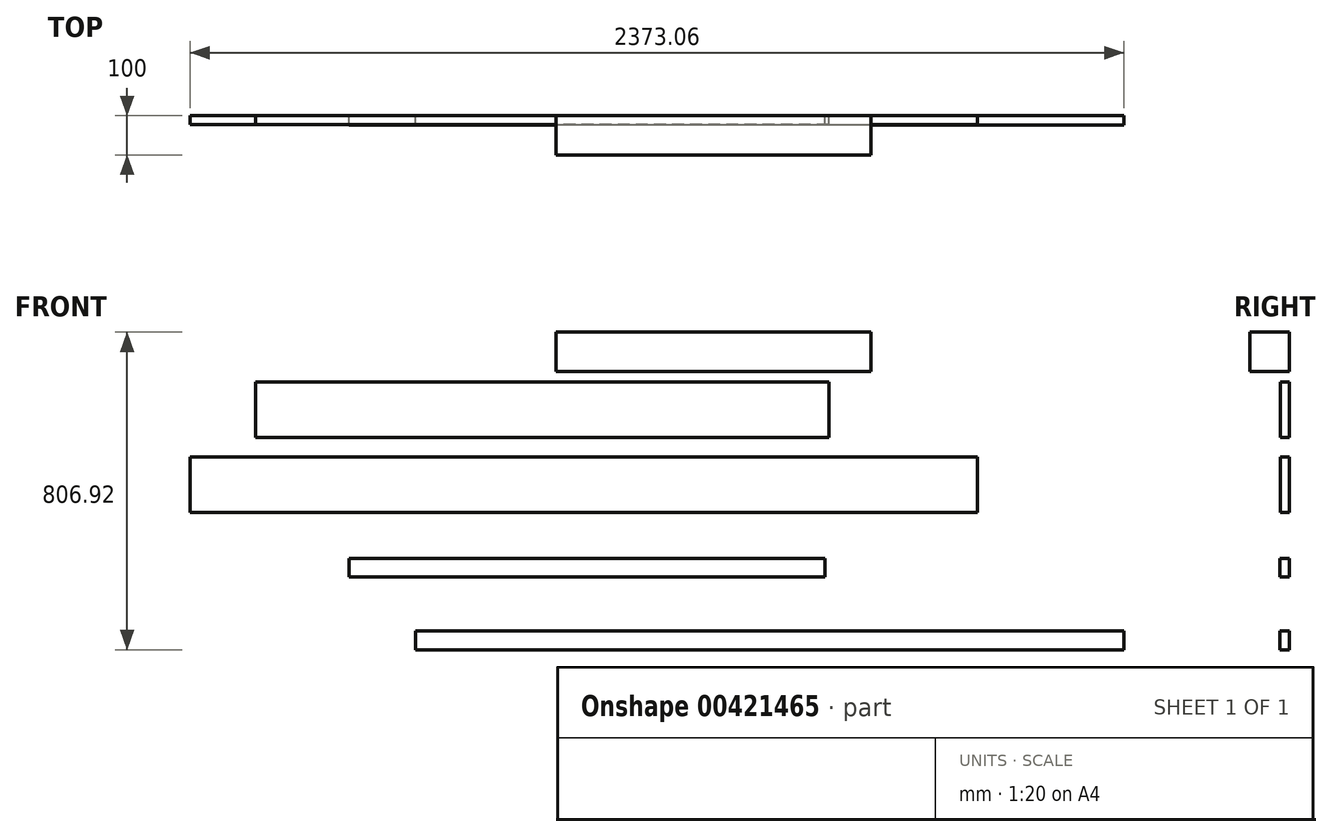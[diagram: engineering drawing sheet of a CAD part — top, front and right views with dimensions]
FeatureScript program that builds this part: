
annotation { "Feature Type Name" : "Feature", "Feature Type Description" : "" }
export const myFeature = defineFeature(function(context is Context, id is Id, definition is map)
    precondition{}
    {
        {
            var Q0;
            Q0=qCreatedBy(makeId("Front.planeOp"),FACE);
            var sketch = newSketch(context, id + "F0", { "sketchPlane" : qUnion([Q0])});
            skLineSegment(sketch, "E0.bottom", {"start": v(-999.75, 98.52) * mm, "end": v(1000.25, 98.52) * mm});
            skLineSegment(sketch, "E0.top", {"start": v(-999.75, -41.48) * mm, "end": v(1000.25, -41.48) * mm});
            skLineSegment(sketch, "E0.left", {"start": v(-999.75, 98.52) * mm, "end": v(-999.75, -41.48) * mm});
            skLineSegment(sketch, "E0.right", {"start": v(1000.25, 98.52) * mm, "end": v(1000.25, -41.48) * mm});
            skSolve(sketch);
        }
        {
            var Q0;
            Q0=makeQuery(id+"F0.imprint","IMPRINT",FACE,{"disambiguationData":[TD([[makeQuery(id+"F0.imprint","IMPRINT",EDGE,{"derivedFrom":sQuery(id+"F0.wireOp",EDGE,"E0.bottom")}),-1.0]])]});
            extrude(context, id + "F1", {"entities" : qUnion([Q0]), "depth" : 23 * mm});
        }
        {
            var Q0;
            Q0=qCreatedBy(makeId("Front.planeOp"),FACE);
            var sketch = newSketch(context, id + "F2", { "sketchPlane" : qUnion([Q0])});
            skLineSegment(sketch, "E1.bottom", {"start": v(623.06, 288.83) * mm, "end": v(-832.94, 288.83) * mm});
            skLineSegment(sketch, "E1.top", {"start": v(623.06, 148.83) * mm, "end": v(-832.94, 148.83) * mm});
            skLineSegment(sketch, "E1.left", {"start": v(623.06, 288.83) * mm, "end": v(623.06, 148.83) * mm});
            skLineSegment(sketch, "E1.right", {"start": v(-832.94, 288.83) * mm, "end": v(-832.94, 148.83) * mm});
            skSolve(sketch);
        }
        {
            var Q0;
            Q0 = qSketchRegion(id + "F2", true);
            extrude(context, id + "F3", {"entities" : qUnion([Q0]), "depth" : 23 * mm});
        }
        {
            var Q0;
            Q0=qCreatedBy(makeId("Front.planeOp"),FACE);
            var sketch = newSketch(context, id + "F4", { "sketchPlane" : qUnion([Q0])});
            skLineSegment(sketch, "E2.bottom", {"start": v(-70.34, 315.88) * mm, "end": v(729.66, 315.88) * mm});
            skLineSegment(sketch, "E2.top", {"start": v(-70.34, 415.88) * mm, "end": v(729.66, 415.88) * mm});
            skLineSegment(sketch, "E2.left", {"start": v(-70.34, 315.88) * mm, "end": v(-70.34, 415.88) * mm});
            skLineSegment(sketch, "E2.right", {"start": v(729.66, 315.88) * mm, "end": v(729.66, 415.88) * mm});
            skSolve(sketch);
        }
        {
            var Q0;
            Q0 = qSketchRegion(id + "F4", true);
            extrude(context, id + "F5", {"entities" : qUnion([Q0]), "depth" : 100 * mm});
        }
        {
            var Q0;
            Q0=qCreatedBy(makeId("Front.planeOp"),FACE);
            var sketch = newSketch(context, id + "F6", { "sketchPlane" : qUnion([Q0])});
            skLineSegment(sketch, "E3.bottom", {"start": v(1373.31, -343.04) * mm, "end": v(-426.69, -343.04) * mm});
            skLineSegment(sketch, "E3.top", {"start": v(1373.31, -391.04) * mm, "end": v(-426.69, -391.04) * mm});
            skLineSegment(sketch, "E3.left", {"start": v(1373.31, -343.04) * mm, "end": v(1373.31, -391.04) * mm});
            skLineSegment(sketch, "E3.right", {"start": v(-426.69, -343.04) * mm, "end": v(-426.69, -391.04) * mm});
            skSolve(sketch);
        }
        {
            var Q0;
            Q0 = qSketchRegion(id + "F6", true);
            extrude(context, id + "F7", {"entities" : qUnion([Q0]), "depth" : 24 * mm});
        }
        {
            var Q0;
            Q0=qCreatedBy(makeId("Front.planeOp"),FACE);
            var sketch = newSketch(context, id + "F8", { "sketchPlane" : qUnion([Q0])});
            skLineSegment(sketch, "E4.bottom", {"start": v(613.93, -158.41) * mm, "end": v(-596.07, -158.41) * mm});
            skLineSegment(sketch, "E4.top", {"start": v(613.93, -206.41) * mm, "end": v(-596.07, -206.41) * mm});
            skLineSegment(sketch, "E4.left", {"start": v(613.93, -158.41) * mm, "end": v(613.93, -206.41) * mm});
            skLineSegment(sketch, "E4.right", {"start": v(-596.07, -158.41) * mm, "end": v(-596.07, -206.41) * mm});
            skSolve(sketch);
        }
        {
            var Q0;
            Q0 = qSketchRegion(id + "F8", true);
            extrude(context, id + "F9", {"entities" : qUnion([Q0]), "depth" : 24 * mm});
        }
    });
